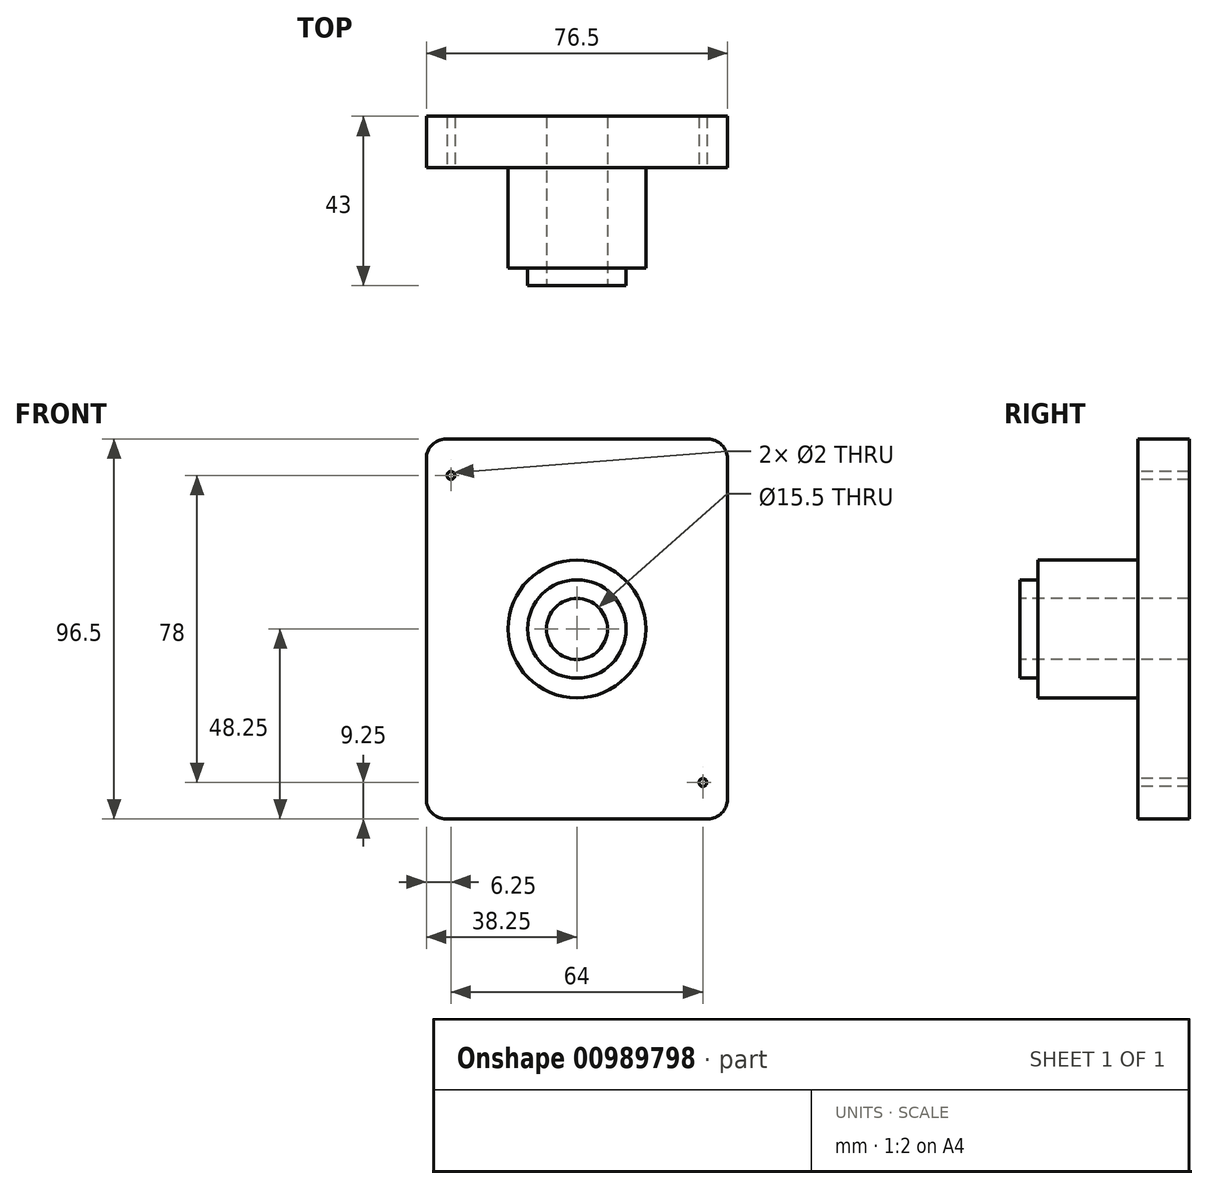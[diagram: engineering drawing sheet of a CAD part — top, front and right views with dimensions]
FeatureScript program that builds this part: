
annotation { "Feature Type Name" : "Feature", "Feature Type Description" : "" }
export const myFeature = defineFeature(function(context is Context, id is Id, definition is map)
    precondition{}
    {
        {
            var Q0;
            Q0=qCreatedBy(makeId("Front.planeOp"),FACE);
            var sketch = newSketch(context, id + "F0", { "sketchPlane" : qUnion([Q0])});
            skLineSegment(sketch, "E0.bottom", {"start": v(0, 0) * mm, "end": v(76.5, 0) * mm});
            skLineSegment(sketch, "E0.top", {"start": v(0, 96.5) * mm, "end": v(76.5, 96.5) * mm});
            skLineSegment(sketch, "E0.left", {"start": v(0, 0) * mm, "end": v(0, 96.5) * mm});
            skLineSegment(sketch, "E0.right", {"start": v(76.5, 0) * mm, "end": v(76.5, 96.5) * mm});
            skSolve(sketch);
        }
        {
            var Q0;
            Q0 = qSketchRegion(id + "F0", true);
            extrude(context, id + "F1", {"entities" : qUnion([Q0]), "depth" : 13 * mm, "offsetDistance" : 25 * mm});
        }
        {
            var Q0;
            Q0=makeQuery(id+"F1.opExtrude","CAP_FACE",FACE,{"disambiguationData":[OSD([sQuery(id+"F0.wireOp",EDGE,"E0.bottom"),sQuery(id+"F0.wireOp",EDGE,"E0.top"),sQuery(id+"F0.wireOp",EDGE,"E0.left"),sQuery(id+"F0.wireOp",EDGE,"E0.right")])],"isStart":false});
            var sketch = newSketch(context, id + "F2", { "sketchPlane" : qUnion([Q0])});
            skCircle(sketch, "E1", {"center": v(38.25, 48.25) * mm, "radius": 17.5 * mm});
            skPoint(sketch, "E2", {"position": v(0, 48.25) * mm});
            skPoint(sketch, "E3", {"position": v(38.25, 96.5) * mm});
            skSolve(sketch);
        }
        {
            var Q0;
            Q0 = qSketchRegion(id + "F2", true);
            extrude(context, id + "F3", {"entities" : qUnion([Q0]), "operationType" : NewBodyOperationType.ADD, "depth" : 30 * mm, "offsetDistance" : 25 * mm});
        }
        {
            var Q0;
            Q0=makeQuery(id+"F1.opExtrude","SWEPT_EDGE",EDGE,{"disambiguationData":[OSD([sQuery(id+"F0.wireOp",EDGE,"E0.top"),sQuery(id+"F0.wireOp",EDGE,"E0.right")])]});
            var Q1;
            Q1=makeQuery(id+"F1.opExtrude","SWEPT_EDGE",EDGE,{"disambiguationData":[OSD([sQuery(id+"F0.wireOp",EDGE,"E0.top"),sQuery(id+"F0.wireOp",EDGE,"E0.left")])]});
            var Q2;
            Q2=makeQuery(id+"F1.opExtrude","SWEPT_EDGE",EDGE,{"disambiguationData":[OSD([sQuery(id+"F0.wireOp",EDGE,"E0.bottom"),sQuery(id+"F0.wireOp",EDGE,"E0.left")])]});
            var Q3;
            Q3=makeQuery(id+"F1.opExtrude","SWEPT_EDGE",EDGE,{"disambiguationData":[OSD([sQuery(id+"F0.wireOp",EDGE,"E0.bottom"),sQuery(id+"F0.wireOp",EDGE,"E0.right")])]});
            fillet(context, id + "F4", {"entities" : qUnion([Q0, Q1, Q2, Q3]), "radius" : 5 * mm, "tangentPropagation" : true, "allowEdgeOverflow" : false});
        }
        {
            var Q0;
            Q0=makeQuery(id+"F3.opExtrude","CAP_FACE",FACE,{"disambiguationData":[OSD([sQuery(id+"F2.wireOp",EDGE,"E1")])],"isStart":false});
            var sketch = newSketch(context, id + "F5", { "sketchPlane" : qUnion([Q0])});
            skCircle(sketch, "E4", {"center": v(38.25, 48.25) * mm, "radius": 12.5 * mm});
            skCircle(sketch, "E5", {"center": v(38.25, 48.25) * mm, "radius": 17.5 * mm});
            skSolve(sketch);
        }
        {
            var Q0;
            Q0 = qSketchRegion(id + "F5", true);
            extrude(context, id + "F6", {"entities" : qUnion([Q0]), "operationType" : NewBodyOperationType.REMOVE, "oppositeDirection" : true, "depth" : 4.5 * mm, "offsetDistance" : 25 * mm});
        }
        {
            var Q0;
            Q0=makeQuery(id+"F3.opExtrude","CAP_FACE",FACE,{"disambiguationData":[OSD([sQuery(id+"F2.wireOp",EDGE,"E1")])],"isStart":false});
            var sketch = newSketch(context, id + "F7", { "sketchPlane" : qUnion([Q0])});
            skCircle(sketch, "E6", {"center": v(38.25, 48.25) * mm, "radius": 7.75 * mm});
            skSolve(sketch);
        }
        {
            var Q0;
            Q0 = qSketchRegion(id + "F7", true);
            var Q1;
            Q1=makeQuery(id+"F1.opExtrude","CAP_FACE",FACE,{"disambiguationData":[OSD([sQuery(id+"F0.wireOp",EDGE,"E0.bottom"),sQuery(id+"F0.wireOp",EDGE,"E0.top"),sQuery(id+"F0.wireOp",EDGE,"E0.left"),sQuery(id+"F0.wireOp",EDGE,"E0.right")])],"isStart":true});
            extrude(context, id + "F8", {"entities" : qUnion([Q0]), "operationType" : NewBodyOperationType.REMOVE, "endBound" : BoundingType.UP_TO_SURFACE, "oppositeDirection" : true, "depth" : 25 * mm, "endBoundEntityFace" : qUnion([Q1]), "offsetDistance" : 25 * mm});
        }
        {
            var Q0;
            Q0=makeQuery(id+"F1.opExtrude","CAP_FACE",FACE,{"disambiguationData":[OSD([sQuery(id+"F0.wireOp",EDGE,"E0.bottom"),sQuery(id+"F0.wireOp",EDGE,"E0.top"),sQuery(id+"F0.wireOp",EDGE,"E0.left"),sQuery(id+"F0.wireOp",EDGE,"E0.right")])],"isStart":false});
            var sketch = newSketch(context, id + "F9", { "sketchPlane" : qUnion([Q0])});
            skLineSegment(sketch, "E7", {"start": v(38.25, 96.5) * mm, "end": v(38.25, 0) * mm, "construction": true});
            skCircle(sketch, "E8.MirrorC", {"center": v(6.25, 87.25) * mm, "radius": 1 * mm});
            skCircle(sketch, "E9.MirrorC", {"center": v(70.25, 9.25) * mm, "radius": 1 * mm});
            skSolve(sketch);
        }
        {
            var Q0;
            Q0 = qSketchRegion(id + "F9", true);
            var Q1;
            Q1=makeQuery(id+"F1.opExtrude","CAP_FACE",FACE,{"disambiguationData":[OSD([sQuery(id+"F0.wireOp",EDGE,"E0.bottom"),sQuery(id+"F0.wireOp",EDGE,"E0.top"),sQuery(id+"F0.wireOp",EDGE,"E0.left"),sQuery(id+"F0.wireOp",EDGE,"E0.right")])],"isStart":true});
            extrude(context, id + "F10", {"entities" : qUnion([Q0]), "operationType" : NewBodyOperationType.REMOVE, "endBound" : BoundingType.UP_TO_SURFACE, "oppositeDirection" : true, "depth" : 25 * mm, "endBoundEntityFace" : qUnion([Q1]), "offsetDistance" : 25 * mm});
        }
    });
